# Revit family: Bike_Rack-Saris_Parking-Bike_Trac
name_source: partatom
category: Site
revit_build: Autodesk Revit 2014 (Build: 20140709_2115(x64)
units: mm (PartAtom-declared; Revit-internal decimal feet)

## types (3) — shared parameters
Assembly Code = G2040500
Ceiling Clearance = 80 Inches Minimum Ceiling Height
Default Elevation = 48 "
Description = Vertical bike parking with variety of security options
Height = 53.4 "
Manufacturer = Saris Parking
Mount Color = Paint - Saris Parking - Powder Coat - Shuttle Black
Number of Parkable Bikes = 1
Product Documentation Link = https://www.sarisparking.com
Product Page URL = https://www.sarisparking.com
URL = https://www.sarisparking.com

## per-type parameters (varying)
| type | Bike Trac Cable Lock | Bike Trac Locking | Length | Weight | Width |
| 6006 | No | Yes | 18.6 " | 16.70 kip | 4.9 " |
| 6003C | Yes | No | 5.3 " | 10.00 kip | 2.9 " |
| 6003T | No | No | 5.3 " | 9.00 kip | 2.9 " |

note: column(s) folded — value = type name in every type: Model

## geometry (parser evidence)
native form markers: Sweep x21
no freeform markers — native parametric forms only
